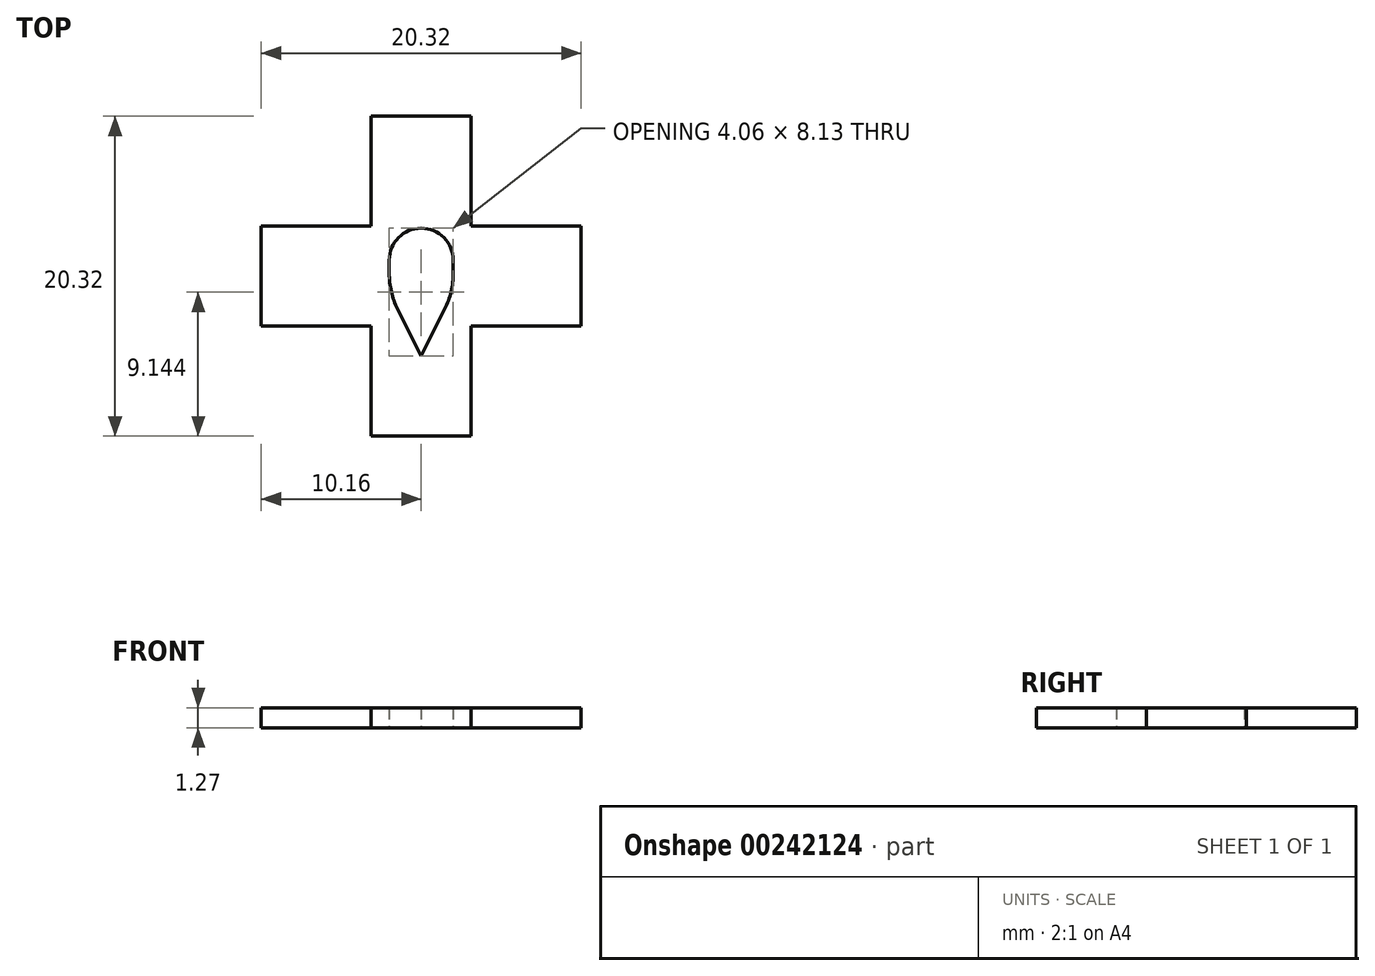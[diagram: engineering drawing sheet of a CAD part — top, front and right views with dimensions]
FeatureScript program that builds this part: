
annotation { "Feature Type Name" : "Feature", "Feature Type Description" : "" }
export const myFeature = defineFeature(function(context is Context, id is Id, definition is map)
    precondition{}
    {
        {
            var Q0;
            Q0=qCreatedBy(makeId("Top.planeOp"),FACE);
            var sketch = newSketch(context, id + "F0", { "sketchPlane" : qUnion([Q0])});
            skLineSegment(sketch, "E0.bottom", {"start": v(-3.17, 10.16) * mm, "end": v(3.17, 10.16) * mm});
            skLineSegment(sketch, "E0.top", {"start": v(-3.17, -10.16) * mm, "end": v(3.17, -10.16) * mm});
            skLineSegment(sketch, "E0.left", {"start": v(-3.18, 10.16) * mm, "end": v(-3.18, 3.18) * mm});
            skLineSegment(sketch, "E0.right", {"start": v(3.17, 10.16) * mm, "end": v(3.17, 3.18) * mm});
            skLineSegment(sketch, "E1.bottom", {"start": v(-10.16, 3.18) * mm, "end": v(-3.17, 3.18) * mm});
            skLineSegment(sketch, "E1.top", {"start": v(-10.16, -3.17) * mm, "end": v(-3.17, -3.17) * mm});
            skLineSegment(sketch, "E1.left", {"start": v(-10.16, 3.18) * mm, "end": v(-10.16, -3.17) * mm});
            skLineSegment(sketch, "E1.right", {"start": v(10.16, 3.18) * mm, "end": v(10.16, -3.17) * mm});
            skLineSegment(sketch, "E2.trimOffspring", {"start": v(3.17, 3.18) * mm, "end": v(10.16, 3.18) * mm});
            skLineSegment(sketch, "E3.trimOffspring", {"start": v(3.17, -3.17) * mm, "end": v(3.17, -10.16) * mm});
            skLineSegment(sketch, "E4.trimOffspring", {"start": v(-3.17, -3.17) * mm, "end": v(-3.17, -10.16) * mm});
            skLineSegment(sketch, "E5.trimOffspring", {"start": v(3.17, -3.17) * mm, "end": v(10.16, -3.17) * mm});
            skLineSegment(sketch, "E6", {"start": v(-2.03, 1.02) * mm, "end": v(-2.03, 0.18) * mm});
            skLineSegment(sketch, "E7", {"start": v(2.03, 1.02) * mm, "end": v(2.03, 0.18) * mm});
            skArc(sketch, "E8", {"start": v(2.03, 1.02) * mm, "mid": v(0, 3.05) * mm, "end": v(-2.03, 1.02) * mm});
            skLineSegment(sketch, "E9", {"start": v(-1.5, -2.09) * mm, "end": v(0, -5.08) * mm});
            skLineSegment(sketch, "E10", {"start": v(0, -5.08) * mm, "end": v(1.5, -2.09) * mm});
            skPoint(sketch, "E11.visualSharp", {"position": v(-2.03, -1.02) * mm});
            skArc(sketch, "E11.filletArc", {"start": v(-2.03, 0.18) * mm, "mid": v(-1.9, -0.98) * mm, "end": v(-1.5, -2.09) * mm});
            skPoint(sketch, "E12.visualSharp", {"position": v(2.03, -1.02) * mm});
            skArc(sketch, "E12.filletArc", {"start": v(1.5, -2.09) * mm, "mid": v(1.9, -0.98) * mm, "end": v(2.03, 0.18) * mm});
            skSolve(sketch);
        }
        {
            var Q0;
            Q0=makeQuery(id+"F0.imprint","IMPRINT",FACE,{"disambiguationData":[TD([[makeQuery(id+"F0.imprint","IMPRINT",EDGE,{"derivedFrom":sQuery(id+"F0.wireOp",EDGE,"E0.bottom")}),-1.0]])]});
            extrude(context, id + "F1", {"entities" : qUnion([Q0]), "depth" : 1.27 * mm});
        }
    });
